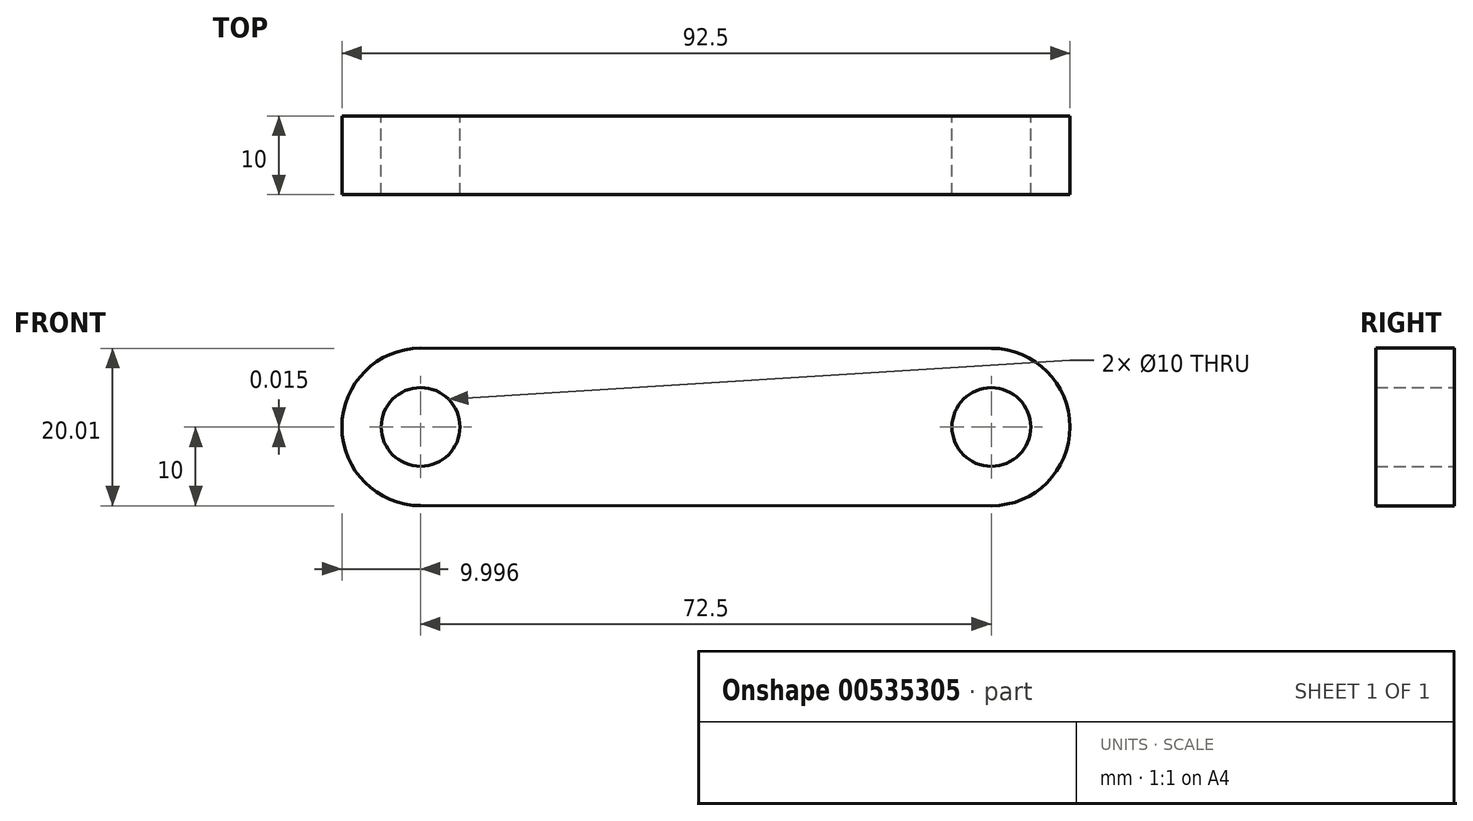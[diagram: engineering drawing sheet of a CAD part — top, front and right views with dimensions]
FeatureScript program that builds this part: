
annotation { "Feature Type Name" : "Feature", "Feature Type Description" : "" }
export const myFeature = defineFeature(function(context is Context, id is Id, definition is map)
    precondition{}
    {
        {
            var Q0;
            Q0=qCreatedBy(makeId("Front.planeOp"),FACE);
            var sketch = newSketch(context, id + "F0", { "sketchPlane" : qUnion([Q0])});
            skCircle(sketch, "E0", {"center": v(42.35, 0) * mm, "radius": 5 * mm});
            skArc(sketch, "E1", {"start": v(42.34, -10) * mm, "mid": v(52.35, 0) * mm, "end": v(42.35, 10) * mm});
            skCircle(sketch, "E2", {"center": v(-30.15, 0.01) * mm, "radius": 5 * mm});
            skArc(sketch, "E3", {"start": v(-30.15, 10.01) * mm, "mid": v(-40.15, 0.02) * mm, "end": v(-30.16, -9.99) * mm});
            skLineSegment(sketch, "E4", {"start": v(-30.15, 10.01) * mm, "end": v(42.35, 10) * mm});
            skLineSegment(sketch, "E5", {"start": v(-30.16, -9.99) * mm, "end": v(42.34, -10) * mm});
            skSolve(sketch);
        }
        {
            var Q0;
            Q0 = qSketchRegion(id + "F0", true);
            extrude(context, id + "F1", {"entities" : qUnion([Q0]), "depth" : 10 * mm, "offsetDistance" : 25 * mm});
        }
    });
